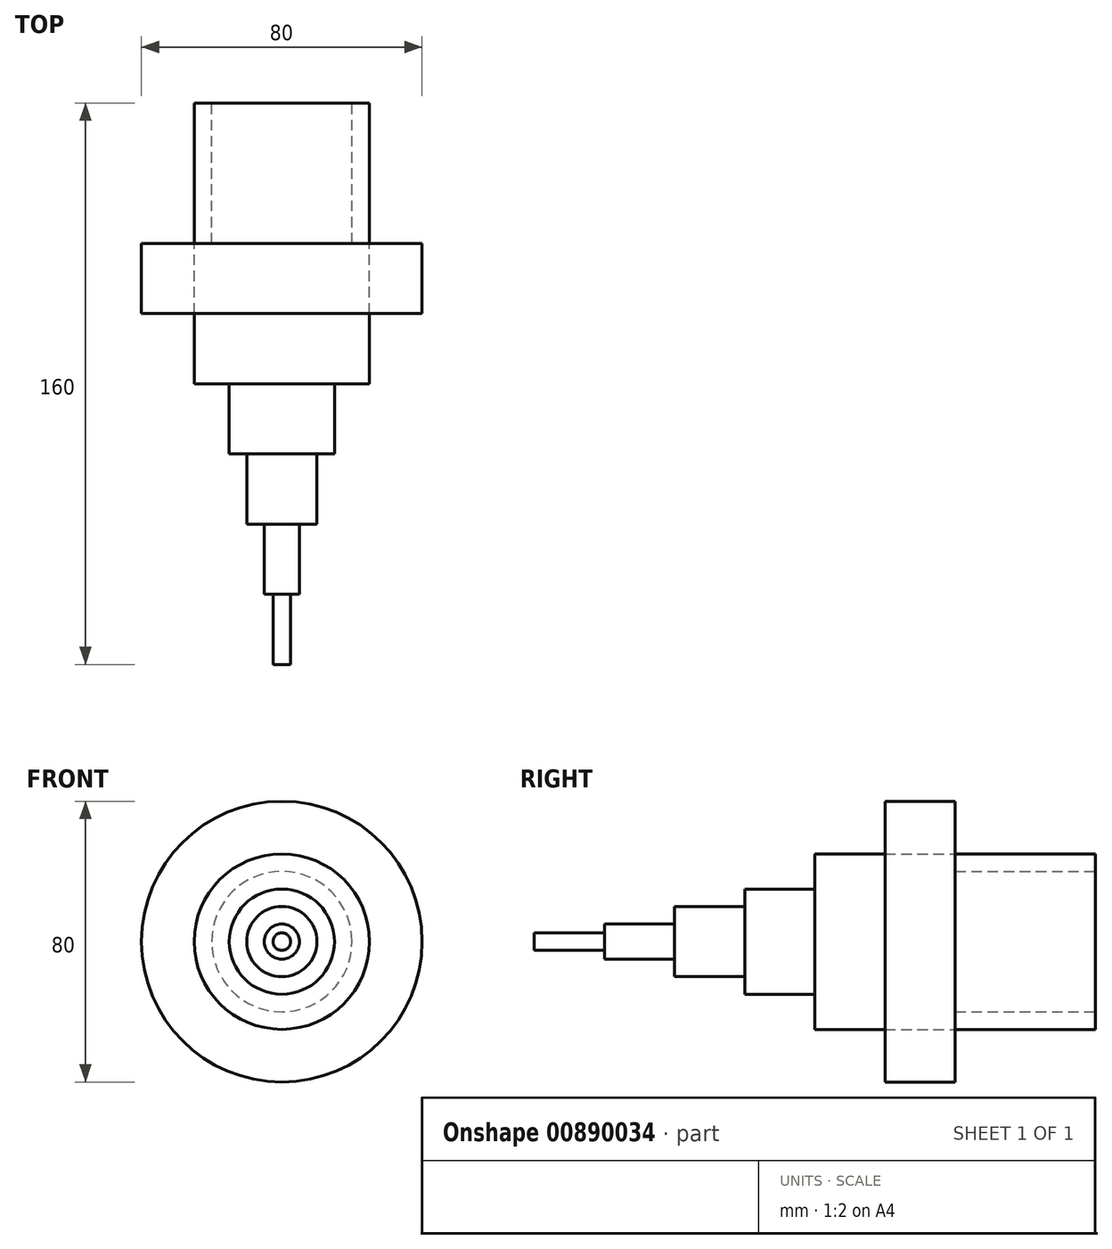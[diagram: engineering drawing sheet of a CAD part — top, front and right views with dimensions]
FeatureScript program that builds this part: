
annotation { "Feature Type Name" : "Feature", "Feature Type Description" : "" }
export const myFeature = defineFeature(function(context is Context, id is Id, definition is map)
    precondition{}
    {
        {
            var Q0;
            Q0=qCreatedBy(makeId("Front.planeOp"),FACE);
            var sketch = newSketch(context, id + "F0", { "sketchPlane" : qUnion([Q0])});
            skCircle(sketch, "E0", {"center": v(0, 0) * mm, "radius": 25 * mm});
            skSolve(sketch);
        }
        {
            var Q0;
            Q0=makeQuery(id+"F0.imprint","IMPRINT",FACE,{"disambiguationData":[TD([[makeQuery(id+"F0.imprint","IMPRINT",EDGE,{"derivedFrom":sQuery(id+"F0.wireOp",EDGE,"E0")}),1.0]])]});
            extrude(context, id + "F1", {"entities" : qUnion([Q0]), "depth" : 20 * mm, "offsetDistance" : 25.4 * mm});
        }
        {
            var Q0;
            Q0=makeQuery(id+"F1.opExtrude","CAP_FACE",FACE,{"disambiguationData":[OSD([sQuery(id+"F0.wireOp",EDGE,"E0")])],"isStart":true});
            extrude(context, id + "F2", {"entities" : qUnion([Q0]), "operationType" : NewBodyOperationType.ADD, "depth" : 20 * mm, "offsetDistance" : 25.4 * mm});
        }
        {
            var Q0;
            Q0=makeQuery(id+"F1.opExtrude","CAP_FACE",FACE,{"disambiguationData":[OSD([sQuery(id+"F0.wireOp",EDGE,"E0")])],"isStart":false});
            var sketch = newSketch(context, id + "F3", { "sketchPlane" : qUnion([Q0])});
            skCircle(sketch, "E1", {"center": v(0, 0) * mm, "radius": 40 * mm});
            skSolve(sketch);
        }
        {
            var Q0;
            Q0=makeQuery(id+"F3.imprint","IMPRINT",FACE,{"disambiguationData":[TD([[makeQuery(id+"F3.imprint","IMPRINT",EDGE,{"derivedFrom":sQuery(id+"F3.wireOp",EDGE,"E1")}),1.0]])]});
            extrude(context, id + "F4", {"entities" : qUnion([Q0]), "depth" : 20 * mm, "offsetDistance" : 25.4 * mm});
        }
        {
            var Q0;
            Q0=makeQuery(id+"F4.opExtrude","CAP_FACE",FACE,{"disambiguationData":[OSD([sQuery(id+"F0.wireOp",EDGE,"E0"),sQuery(id+"F3.wireOp",EDGE,"E1")])],"isStart":false});
            var sketch = newSketch(context, id + "F5", { "sketchPlane" : qUnion([Q0])});
            skCircle(sketch, "E2", {"center": v(0, 0) * mm, "radius": 25 * mm});
            skSolve(sketch);
        }
        {
            var Q0;
            Q0 = qSketchRegion(id + "F5", true);
            extrude(context, id + "F6", {"entities" : qUnion([Q0]), "depth" : 20 * mm, "offsetDistance" : 25.4 * mm});
        }
        {
            var Q0;
            Q0=makeQuery(id+"F2.opExtrude","CAP_FACE",FACE,{"disambiguationData":[OSD([sQuery(id+"F0.wireOp",EDGE,"E0")])],"isStart":false});
            var sketch = newSketch(context, id + "F7", { "sketchPlane" : qUnion([Q0])});
            skCircle(sketch, "E3", {"center": v(0, 0) * mm, "radius": 20 * mm});
            skSolve(sketch);
        }
        {
            var Q0;
            Q0 = qSketchRegion(id + "F7", true);
            extrude(context, id + "F8", {"entities" : qUnion([Q0]), "operationType" : NewBodyOperationType.REMOVE, "oppositeDirection" : true, "depth" : 40 * mm, "offsetDistance" : 25.4 * mm});
        }
        {
            var Q0;
            Q0=makeQuery(id+"F6.opExtrude","CAP_FACE",FACE,{"disambiguationData":[OSD([sQuery(id+"F5.wireOp",EDGE,"E2")])],"isStart":false});
            var sketch = newSketch(context, id + "F9", { "sketchPlane" : qUnion([Q0])});
            skCircle(sketch, "E4", {"center": v(0, 0) * mm, "radius": 15 * mm});
            skSolve(sketch);
        }
        {
            var Q0;
            Q0 = qSketchRegion(id + "F9", true);
            extrude(context, id + "F10", {"entities" : qUnion([Q0]), "operationType" : NewBodyOperationType.ADD, "depth" : 20 * mm, "offsetDistance" : 25.4 * mm});
        }
        {
            var Q0;
            Q0=makeQuery(id+"F10.opExtrude","CAP_FACE",FACE,{"disambiguationData":[OSD([sQuery(id+"F9.wireOp",EDGE,"E4")])],"isStart":false});
            var sketch = newSketch(context, id + "F11", { "sketchPlane" : qUnion([Q0])});
            skCircle(sketch, "E5", {"center": v(0, 0) * mm, "radius": 10 * mm});
            skSolve(sketch);
        }
        {
            var Q0;
            Q0 = qSketchRegion(id + "F11", true);
            extrude(context, id + "F12", {"entities" : qUnion([Q0]), "operationType" : NewBodyOperationType.ADD, "depth" : 20 * mm, "offsetDistance" : 25.4 * mm});
        }
        {
            var Q0;
            Q0=makeQuery(id+"F12.opExtrude","CAP_FACE",FACE,{"disambiguationData":[OSD([sQuery(id+"F11.wireOp",EDGE,"E5")])],"isStart":false});
            var sketch = newSketch(context, id + "F13", { "sketchPlane" : qUnion([Q0])});
            skCircle(sketch, "E6", {"center": v(0, 0) * mm, "radius": 5 * mm});
            skSolve(sketch);
        }
        {
            var Q0;
            Q0 = qSketchRegion(id + "F13", true);
            extrude(context, id + "F14", {"entities" : qUnion([Q0]), "operationType" : NewBodyOperationType.ADD, "depth" : 20 * mm, "offsetDistance" : 25.4 * mm});
        }
        {
            var Q0;
            Q0=makeQuery(id+"F14.opExtrude","CAP_FACE",FACE,{"disambiguationData":[OSD([sQuery(id+"F13.wireOp",EDGE,"E6")])],"isStart":false});
            var sketch = newSketch(context, id + "F15", { "sketchPlane" : qUnion([Q0])});
            skCircle(sketch, "E7", {"center": v(0, 0) * mm, "radius": 2.5 * mm});
            skSolve(sketch);
        }
        {
            var Q0;
            Q0 = qSketchRegion(id + "F15", true);
            extrude(context, id + "F16", {"entities" : qUnion([Q0]), "operationType" : NewBodyOperationType.ADD, "depth" : 20 * mm, "offsetDistance" : 25.4 * mm});
        }
    });
